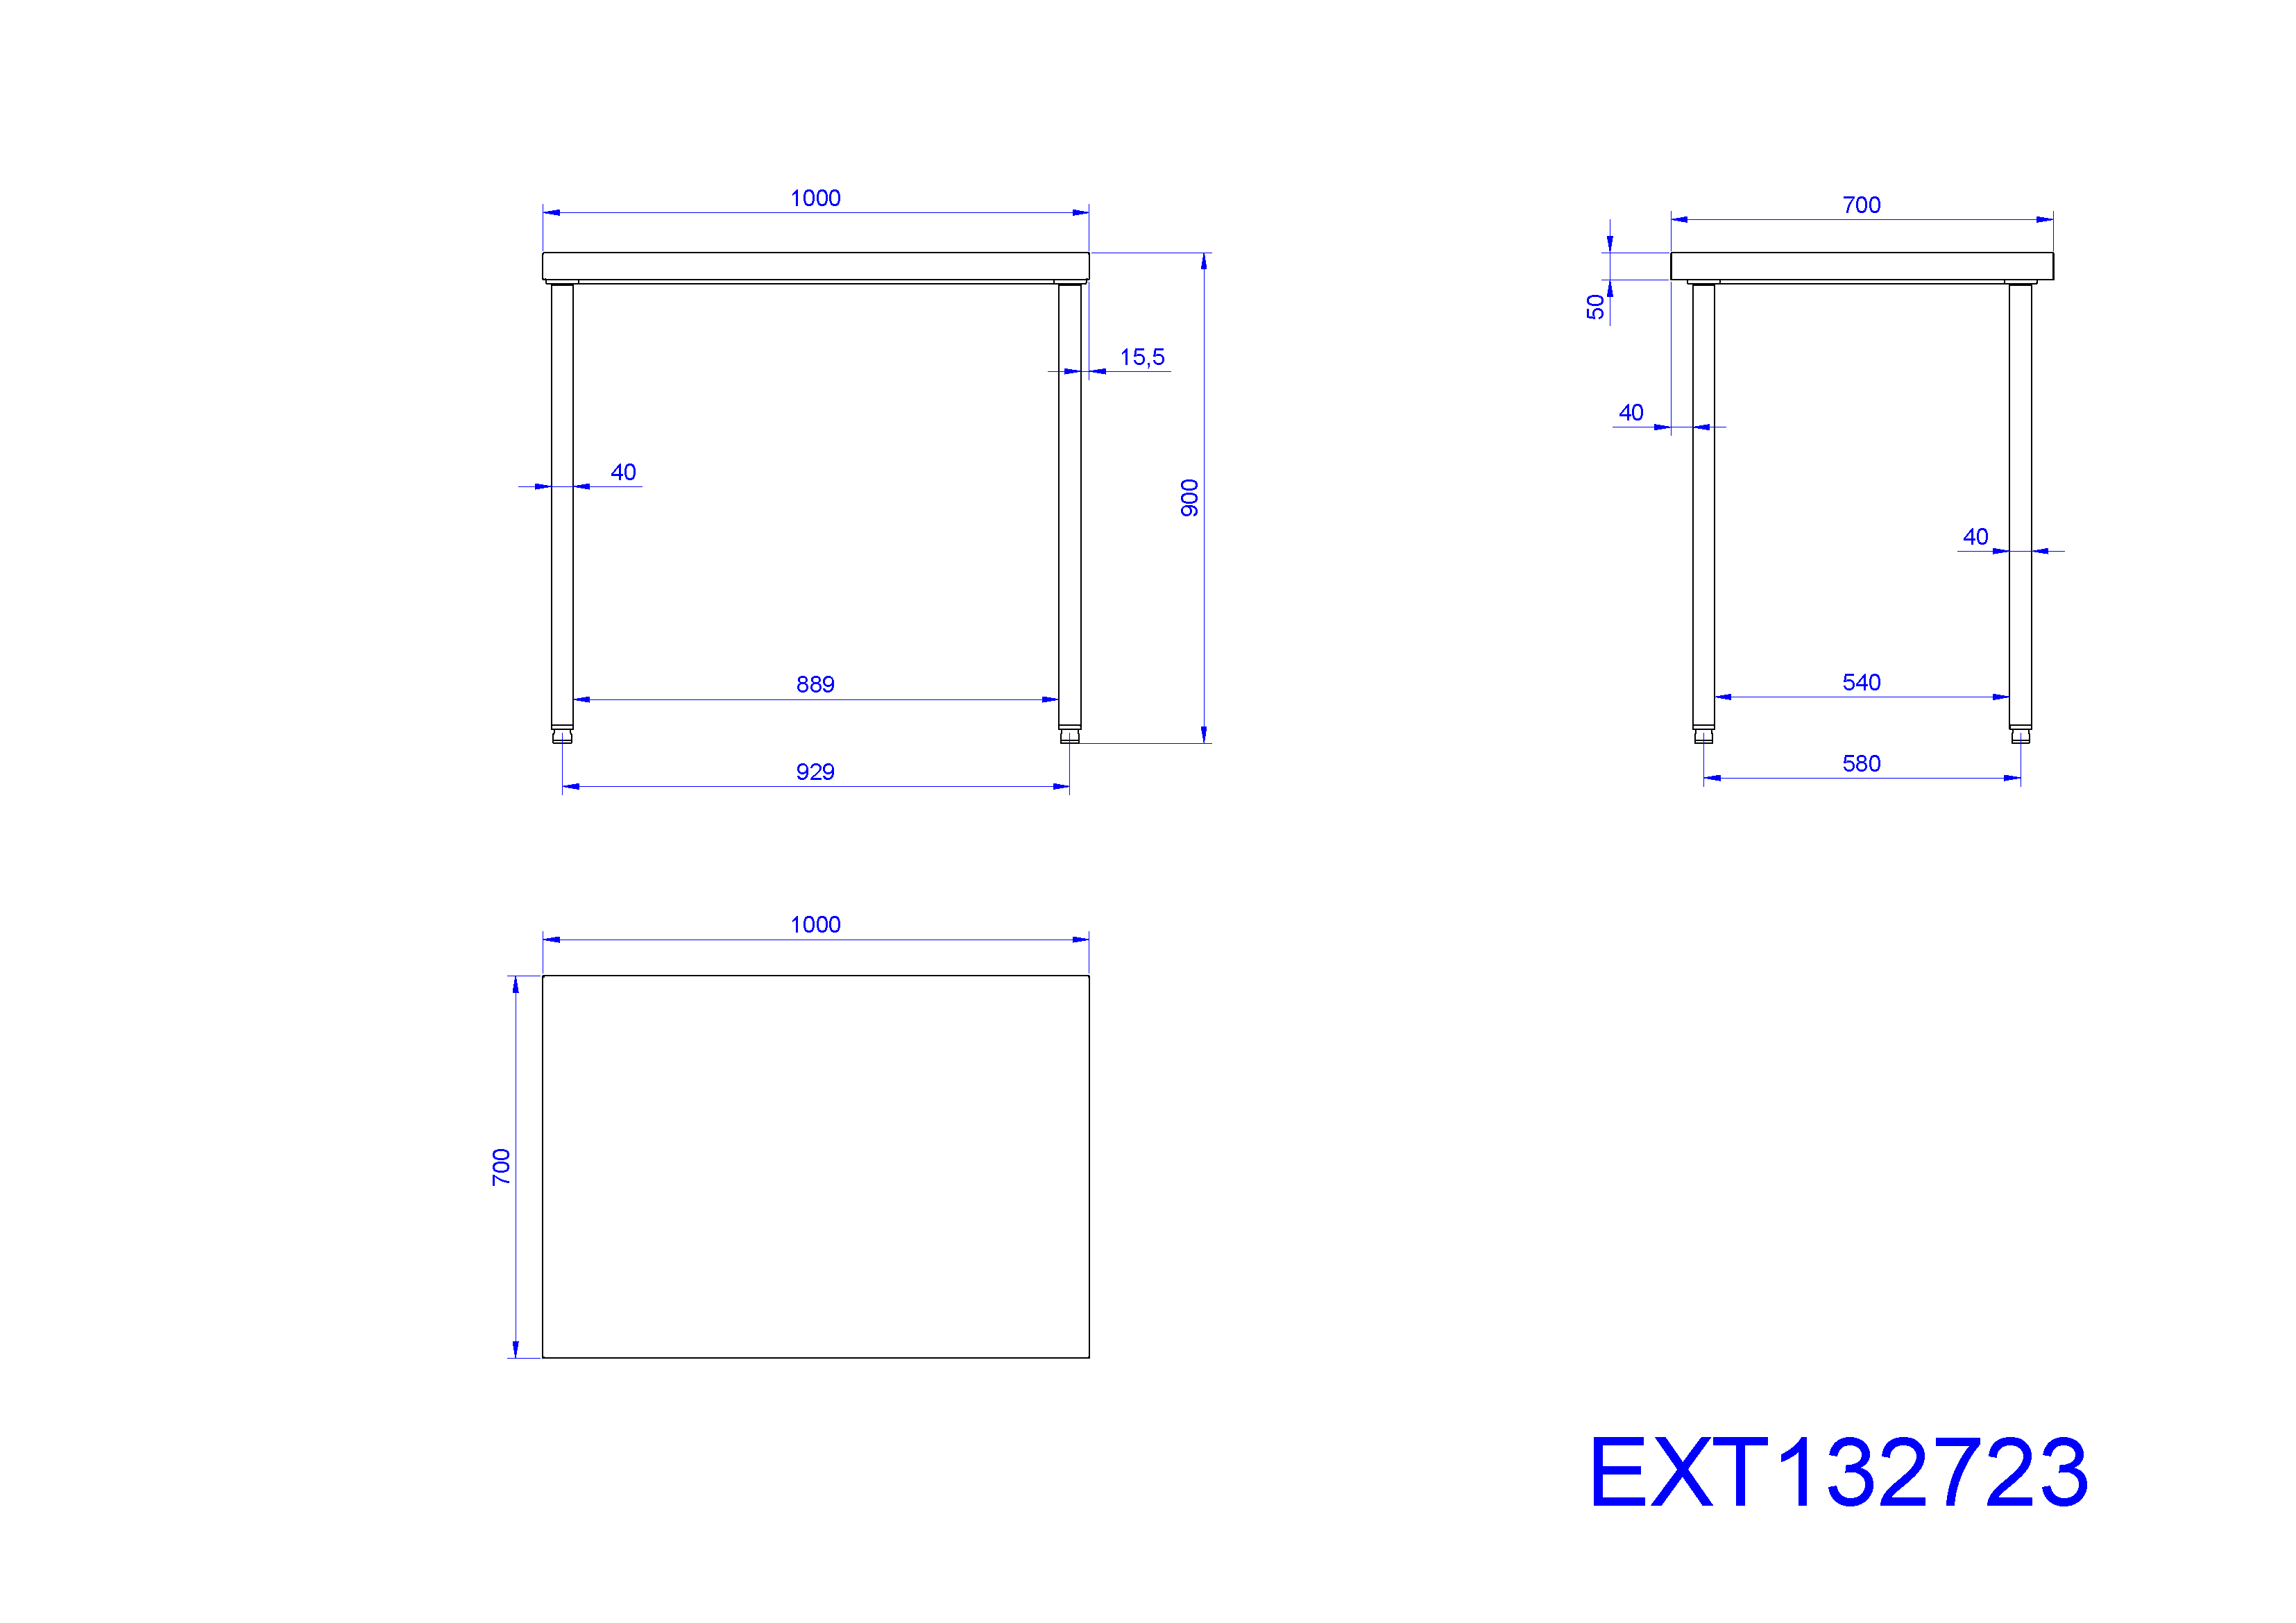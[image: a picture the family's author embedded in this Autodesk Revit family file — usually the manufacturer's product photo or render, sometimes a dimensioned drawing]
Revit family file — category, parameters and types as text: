
# Revit family: QF_ELECTROLUXPROFESSIONAL_133252_MLA2026DXPN
name_source: partatom
category: Attrezzature speciali
units: mm (PartAtom-declared; Revit-internal decimal feet)

## family parameters
Basato su piano di lavoro = No
Condiviso = No
Punto di calcolo locali = No
Quota connettore circolare = Usa diametro
Sempre verticale = Sì
Taglio con vuoti quando caricato = No
Tipo di parte = Normale

## types (1)
- Standard
    Accessory = Sì
    Cold Water Size = 0 mm
    Compressed Air Pressure = 0.0 Pa
    Compressed Air Size = 0 mm
    Compressed Air Volume = 0.0 L/s
    Condensate Return Size = 0 mm
    Cycle = 0 Hz
    Depth Actual = 700 mm  [stored 2.29659 ft]
    Descrizione = CUPB.SINK 2 BOWLS 600X500+R/H DRAIN.2000
    Direct Waste Size = 51 mm
    Gas Input Pressure = 0
    Gas KW = 0
    Gas Size = 0 mm
    HP = 0 HP
    Height Actual = 1000 mm  [stored 3.28084 ft]
    Hot Water Size = 0 mm
    Item Number = 133252
    Length Actual = 2000 mm  [stored 6.56168 ft]
    Modello = MLA2026DXPN
    Phase = 0
    Produttore = Electrolux Professional
    Prospetto di default = 0 mm  [stored 0 ft]
    Refrigerant Compressor Remote = Sì
    Refrigeration Liquid Line Size = 0 mm  [stored 0 ft]
    Refrigeration Suction Line Size = 0 mm  [stored 0 ft]
    Steam Consumption per Hour = 0
    Steam Supply Maximum Pressure = 0.0 Pa
    Steam Supply Minimum Pressure = 0.0 Pa
    Steam Supply Size = 0 mm
    URL = https://www.electroluxprofessional.com
    URL Manufacturer = https://www.electroluxprofessional.com
    Volts = 0 V
    Watts = 0 W
    Weight = 75.00 kg

note: source unit labels omitted for Gas Input Pressure — the stored unit's dimension contradicts the parameter name (converter mislabeling)

note: [stored X ft] marks values corroborated as IEEE doubles in the binary element streams (Revit-internal decimal feet)

## geometry (parser evidence)
native form markers: Blend x4, Sweep x3
no freeform markers — native parametric forms only
